# Revit family: RepeatingDetail_Cladding_Knotwood_Traditional
name_source: partatom
category: Detail Items
units: mm (PartAtom-declared; Revit-internal decimal feet)

## family parameters
Rotate with component = No
Section Shape = Not Defined
Shared = No

## types (3) — shared parameters
Manufacturer = Knotwood
ManufacturerURLProductSpecific = https://www.knotwood.com.au
ModifiedIssue = 20231110 $
URL = https://www.knotwood.com.au

## per-type parameters (varying)
| type | CladdingBoardTypeSelector | CoverWidth | Description | ManufacturerSpecCode | Model |
| 100mm (KEC100LW) | DetailItem_Cladding_Knotwood_Traditional : 100mm (KEC100LW) | 100 mm  [stored 0.328084 ft] | Knotwood Cladding (KEC100LW) | KEC100LW | KEC100LW |
| 150mm (KEC150LW) | DetailItem_Cladding_Knotwood_Traditional : 150mm (KEC150LW) | 150 mm | Knotwood Cladding (KEC150LW) | KEC150LW | KEC150LW |
| 200mm (KEC200LW) | DetailItem_Cladding_Knotwood_Traditional : 200mm (KEC200LW) | 200 mm  [stored 0.656168 ft] | Knotwood Cladding (KEC200LW) | KEC200LW | KEC200LW |

note: [stored X ft] marks values corroborated as IEEE doubles in the binary element streams (Revit-internal decimal feet)

## geometry (parser evidence)
native form markers: Sweep x2
no freeform markers — native parametric forms only
